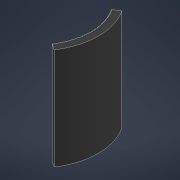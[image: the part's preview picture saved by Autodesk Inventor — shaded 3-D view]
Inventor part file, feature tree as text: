
AUTODESK INVENTOR PART (.ipt)
format: ipt  version: 2021 (Build 250183000, 183)  size: 195,072 bytes
history: native  units: mm
features: extrude x2, sketch x2, pattern_circular x1
ambient origin geometry x8: Origin, YZ Plane, XZ Plane, XY Plane, X Axis, Y Axis, Z Axis, Center Point
bodies: Solid1 (feature_tree)
feature tree (5):
  extrude  "Extrusion1"  Depth=12.133mm
  extrude  "Extrusion2"  Depth=20.0mm
  pattern_circular  "Circular Pattern1"  [2 undecoded]
  sketch  "Sketch1"  dims[d0=12.133mm d2=12.133mm]
  sketch  "Sketch2"  dims[d3=0.0mm d5=2.0mm d6=2.0mm d7=1.5mm d8=20.0mm d9=0.0mm d11=0.1mm d12=10.0mm d13=5.823721mm d14=20.0mm d15=0.145593mm d16=0.0mm d17=0.0mm d18=400.0mm d19=11.657054mm]
note: 2 required parameter values undecoded (feature->parameter linkage not recoverable at this tier; creation-order binding heuristic only, values carry confidence <= 0.55)
